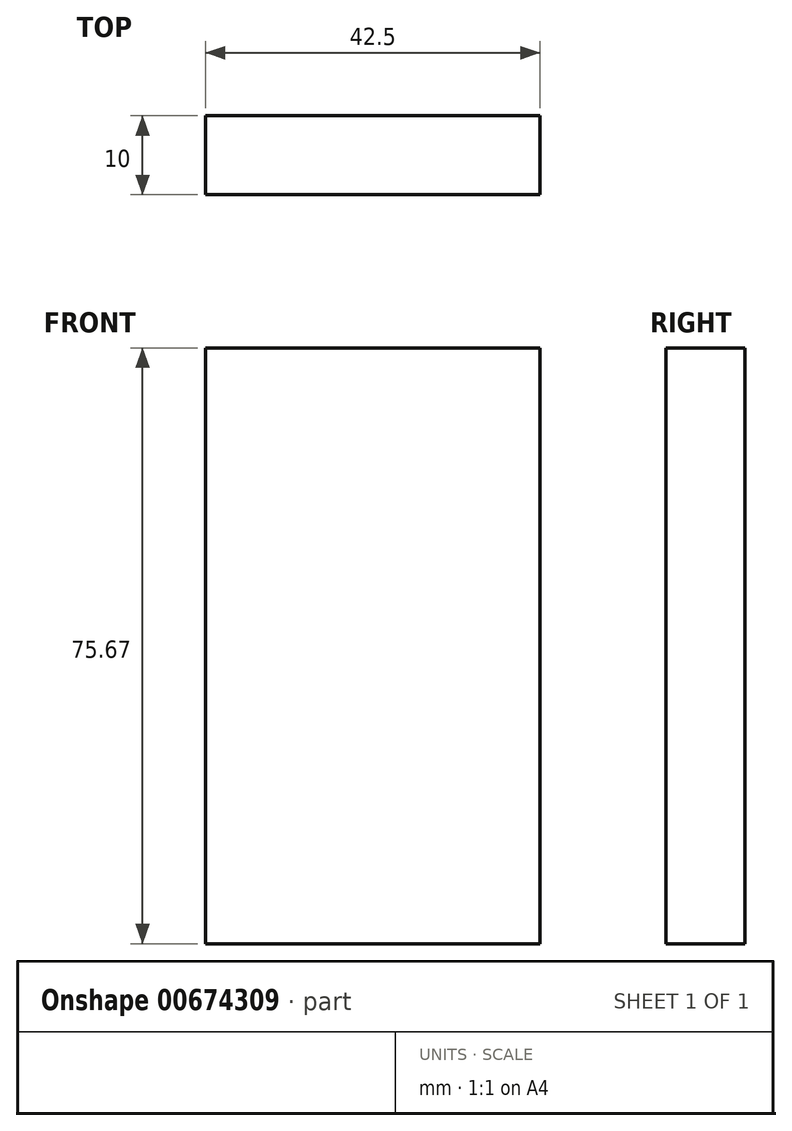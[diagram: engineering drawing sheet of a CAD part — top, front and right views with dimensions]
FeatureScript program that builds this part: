
annotation { "Feature Type Name" : "Feature", "Feature Type Description" : "" }
export const myFeature = defineFeature(function(context is Context, id is Id, definition is map)
    precondition{}
    {
        {
            var Q0;
            Q0=qCreatedBy(makeId("Front.planeOp"),FACE);
            var sketch = newSketch(context, id + "F0", { "sketchPlane" : qUnion([Q0])});
            skLineSegment(sketch, "E0.bottom", {"start": v(-21.25, 42.36) * mm, "end": v(21.25, 42.36) * mm});
            skLineSegment(sketch, "E0.top", {"start": v(-21.25, -33.3) * mm, "end": v(21.25, -33.3) * mm});
            skLineSegment(sketch, "E0.left", {"start": v(-21.25, 42.36) * mm, "end": v(-21.25, -33.3) * mm});
            skLineSegment(sketch, "E0.right", {"start": v(21.25, 42.36) * mm, "end": v(21.25, -33.3) * mm});
            skSolve(sketch);
        }
        {
            var Q0;
            Q0 = qSketchRegion(id + "F0", true);
            extrude(context, id + "F1", {"entities" : qUnion([Q0]), "depth" : 10 * mm, "offsetDistance" : 25 * mm});
        }
    });
